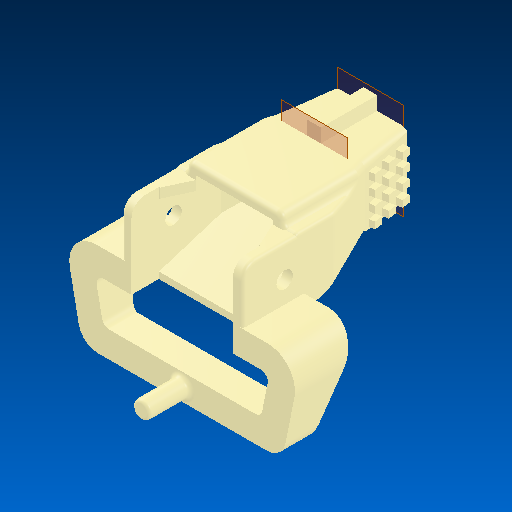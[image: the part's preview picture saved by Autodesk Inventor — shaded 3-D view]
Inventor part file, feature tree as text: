
AUTODESK INVENTOR PART (.ipt)
format: ipt  version: 2025.2 (Build 292293000, 293)  size: 835,584 bytes
history: native  units: in
note: dims shown in document units (in); Inventor stores cm internally (conversion verified against a paired STEP export)
features: plane x8, split x4, mirror x2, direct_edit x1, delete_face x1, boolean_combine x1, other x1, move_body x1
ambient origin geometry x8: Origin, YZ Plane, XZ Plane, XY Plane, X Axis, Y Axis, Z Axis, Center Point
bodies: Solid1 (feature_tree), Solid6 (feature_tree), Body1 (feature_tree), Solid2 (feature_tree), Solid3 (feature_tree), Solid4 (feature_tree), Solid5 (feature_tree)
feature tree (19):
  direct_edit  "Direct Edit1"
  plane  "Work Plane3"
  plane  "Work Plane4"
  split  "Split1"
  plane  "Work Plane5"
  split  "Split2"
  mirror  "Mirror1"
  delete_face  "Delete Face1"
  plane  "Work Plane6"
  mirror  "Mirror2"
  plane  "Work Plane8"
  boolean_combine  "Combine1"
  split  "Split3"
  plane  "Work Plane9"
  split  "Split4"
  plane  "Work Plane2"
  other  "Pattern of Solid4:1"
  plane  "Work Plane7"
  move_body  "Move1"
